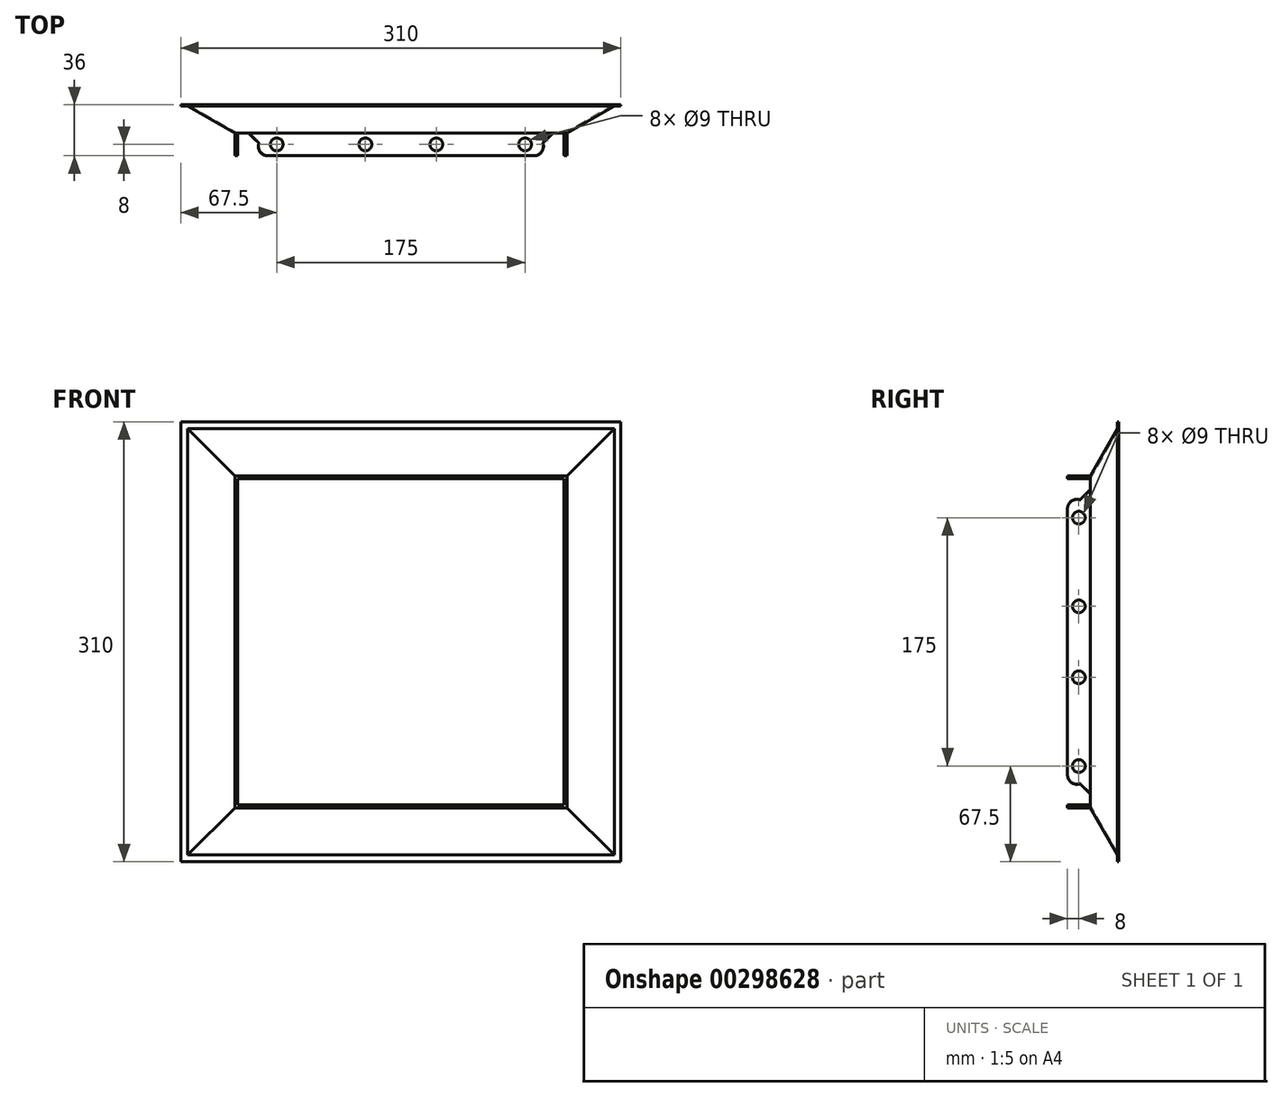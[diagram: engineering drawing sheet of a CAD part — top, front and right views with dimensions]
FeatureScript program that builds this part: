
annotation { "Feature Type Name" : "Feature", "Feature Type Description" : "" }
export const myFeature = defineFeature(function(context is Context, id is Id, definition is map)
    precondition{}
    {
        {
            var Q0;
            Q0=qCreatedBy(makeId("Front.planeOp"),FACE);
            var sketch = newSketch(context, id + "F0", { "sketchPlane" : qUnion([Q0])});
            skLineSegment(sketch, "E0.bottom", {"start": v(-155, 155) * mm, "end": v(155, 155) * mm});
            skLineSegment(sketch, "E0.top", {"start": v(-155, -155) * mm, "end": v(155, -155) * mm});
            skLineSegment(sketch, "E0.left", {"start": v(-155, 155) * mm, "end": v(-155, -155) * mm});
            skLineSegment(sketch, "E0.right", {"start": v(155, 155) * mm, "end": v(155, -155) * mm});
            skLineSegment(sketch, "E1.bottom", {"start": v(150, -150) * mm, "end": v(-150, -150) * mm});
            skLineSegment(sketch, "E1.top", {"start": v(150, 150) * mm, "end": v(-150, 150) * mm});
            skLineSegment(sketch, "E1.left", {"start": v(150, -150) * mm, "end": v(150, 150) * mm});
            skLineSegment(sketch, "E1.right", {"start": v(-150, -150) * mm, "end": v(-150, 150) * mm});
            skPoint(sketch, "E1.middle", {"position": v(0, 0) * mm});
            skSolve(sketch);
        }
        {
            var Q0;
            Q0=makeQuery(id+"F0.imprint","IMPRINT",FACE,{"disambiguationData":[TD([[makeQuery(id+"F0.imprint","IMPRINT",EDGE,{"derivedFrom":sQuery(id+"F0.wireOp",EDGE,"E0.bottom")}),-1.0]])]});
            cPlane(context, id + "F1", {"entities" : qUnion([Q0]), "cplaneType" : CPlaneType.OFFSET, "offset" : 20 * mm, "width" : 150 * mm, "height" : 150 * mm});
        }
        {
            var Q0;
            Q0=qCreatedBy(id+"F1.planeOp",FACE);
            var sketch = newSketch(context, id + "F2", { "sketchPlane" : qUnion([Q0])});
            skLineSegment(sketch, "E2.bottom", {"start": v(115, -115) * mm, "end": v(-115, -115) * mm});
            skLineSegment(sketch, "E2.top", {"start": v(115, 115) * mm, "end": v(-115, 115) * mm});
            skLineSegment(sketch, "E2.left", {"start": v(115, -115) * mm, "end": v(115, 115) * mm});
            skLineSegment(sketch, "E2.right", {"start": v(-115, -115) * mm, "end": v(-115, 115) * mm});
            skPoint(sketch, "E2.middle", {"position": v(0, 0) * mm});
            skSolve(sketch);
        }
        {
            var Q0;
            Q0=makeQuery(id+"F0.imprint","IMPRINT",FACE,{"disambiguationData":[TD([[makeQuery(id+"F0.imprint","IMPRINT",EDGE,{"derivedFrom":sQuery(id+"F0.wireOp",EDGE,"E1.bottom")}),-1.0]])]});
            var Q1;
            Q1=makeQuery(id+"F2.imprint","IMPRINT",FACE,{"disambiguationData":[TD([[makeQuery(id+"F2.imprint","IMPRINT",EDGE,{"derivedFrom":sQuery(id+"F2.wireOp",EDGE,"E2.bottom")}),-1.0]])]});
            loft(context, id + "F3", {"sheetProfilesArray" : [{ "sheetProfileEntities" : qUnion([Q0]) }, { "sheetProfileEntities" : qUnion([Q1]) }]});
        }
        {
            var Q0;
            Q0=makeQuery(id+"F3.opLoft","CAP_FACE",FACE,{"disambiguationData":[OSD([makeQuery(id+"F2.imprint","IMPRINT",FACE,{"disambiguationData":[TD([[makeQuery(id+"F2.imprint","IMPRINT",EDGE,{"derivedFrom":sQuery(id+"F2.wireOp",EDGE,"E2.bottom")}),-1.0]])]})])],"isStart":true});
            var Q1;
            Q1=makeQuery(id+"F3.opLoft","CAP_FACE",FACE,{"disambiguationData":[OSD([makeQuery(id+"F0.imprint","IMPRINT",FACE,{"disambiguationData":[TD([[makeQuery(id+"F0.imprint","IMPRINT",EDGE,{"derivedFrom":sQuery(id+"F0.wireOp",EDGE,"E1.bottom")}),-1.0]])]})])],"isStart":true});
            shell(context, id + "F4", {"entities" : qUnion([Q0, Q1]), "thickness" : 1 * mm, "oppositeDirection" : true});
        }
        {
            var Q0;
            Q0=makeQuery(id+"F0.imprint","IMPRINT",FACE,{"disambiguationData":[TD([[makeQuery(id+"F0.imprint","IMPRINT",EDGE,{"derivedFrom":sQuery(id+"F0.wireOp",EDGE,"E0.bottom")}),-1.0]])]});
            extrude(context, id + "F5", {"entities" : qUnion([Q0]), "operationType" : NewBodyOperationType.ADD, "depth" : 1 * mm});
        }
        {
            var Q0;
            Q0=makeQuery(id+"F3.opLoft","CAP_FACE",FACE,{"disambiguationData":[OSD([makeQuery(id+"F2.imprint","IMPRINT",FACE,{"disambiguationData":[TD([[makeQuery(id+"F2.imprint","IMPRINT",EDGE,{"derivedFrom":sQuery(id+"F2.wireOp",EDGE,"E2.bottom")}),-1.0]])]})])],"isStart":true});
            var sketch = newSketch(context, id + "F6", { "sketchPlane" : qUnion([Q0])});
            skLineSegment(sketch, "E3.0", {"start": v(-115, -115) * mm, "end": v(115, -115) * mm});
            skLineSegment(sketch, "E4.0", {"start": v(115, -115) * mm, "end": v(115, 115) * mm});
            skLineSegment(sketch, "E5.0", {"start": v(117.02, -117.02) * mm, "end": v(117.02, 117.02) * mm});
            skLineSegment(sketch, "E6.0", {"start": v(117.02, 117.02) * mm, "end": v(-117.02, 117.02) * mm});
            skLineSegment(sketch, "E7.0", {"start": v(115, 115) * mm, "end": v(-115, 115) * mm});
            skLineSegment(sketch, "E8.0", {"start": v(-117.02, 117.02) * mm, "end": v(-117.02, -117.02) * mm});
            skLineSegment(sketch, "E9.0", {"start": v(-115, 115) * mm, "end": v(-115, -115) * mm});
            skLineSegment(sketch, "E10.0", {"start": v(-117.02, -117.02) * mm, "end": v(117.02, -117.02) * mm});
            skSolve(sketch);
        }
        {
            var Q0;
            Q0=qSketchRegion(id+"F6",true);
            extrude(context, id + "F7", {"entities" : qUnion([Q0]), "operationType" : NewBodyOperationType.ADD, "depth" : 16 * mm});
        }
        {
            var Q0;
            Q0=makeQuery(id+"F7.opExtrude","SWEPT_FACE",FACE,{"disambiguationData":[OSD([sQuery(id+"F6.wireOp",EDGE,"E6.0")])]});
            var sketch = newSketch(context, id + "F8", { "sketchPlane" : qUnion([Q0])});
            skLineSegment(sketch, "E11", {"start": v(117.02, -20) * mm, "end": v(107.02, -20) * mm});
            skLineSegment(sketch, "E12", {"start": v(107.02, -20) * mm, "end": v(99.94, -27.07) * mm});
            skArc(sketch, "E13", {"start": v(93.63, -36) * mm, "mid": v(99.1, -33.17) * mm, "end": v(99.94, -27.07) * mm});
            skLineSegment(sketch, "E14", {"start": v(117.02, -20) * mm, "end": v(117.02, -36) * mm});
            skLineSegment(sketch, "E15", {"start": v(93.63, -36) * mm, "end": v(117.02, -36) * mm});
            skLineSegment(sketch, "E16", {"start": v(-117.02, -20) * mm, "end": v(-107.02, -20) * mm});
            skLineSegment(sketch, "E17", {"start": v(-107.02, -20) * mm, "end": v(-99.94, -27.07) * mm});
            skArc(sketch, "E18", {"start": v(-99.94, -27.07) * mm, "mid": v(-99.1, -33.17) * mm, "end": v(-93.63, -36) * mm});
            skLineSegment(sketch, "E19", {"start": v(-93.63, -36) * mm, "end": v(-117.02, -36) * mm});
            skLineSegment(sketch, "E20", {"start": v(-117.02, -36) * mm, "end": v(-117.02, -20) * mm});
            skSolve(sketch);
        }
        {
            var Q0;
            Q0=makeQuery(id+"F8.imprint","IMPRINT",FACE,{"disambiguationData":[TD([[makeQuery(id+"F8.imprint","IMPRINT",EDGE,{"derivedFrom":sQuery(id+"F8.wireOp",EDGE,"E11")}),1.0]])]});
            var Q1;
            Q1=sQuery(id+"F8.wireOp",EDGE,"E14");
            revolve(context, id + "F9", {"operationType" : NewBodyOperationType.REMOVE, "entities" : qUnion([Q0]), "axis" : qUnion([Q1]), "revolveType" : RevolveType.FULL, "oppositeDirection" : true});
        }
        {
            var Q0;
            Q0=makeQuery(id+"F8.imprint","IMPRINT",FACE,{"disambiguationData":[TD([[makeQuery(id+"F8.imprint","IMPRINT",EDGE,{"derivedFrom":sQuery(id+"F8.wireOp",EDGE,"E16")}),1.0]])]});
            var Q1;
            Q1=sQuery(id+"F8.wireOp",EDGE,"E20");
            revolve(context, id + "F10", {"operationType" : NewBodyOperationType.REMOVE, "entities" : qUnion([Q0]), "axis" : qUnion([Q1]), "revolveType" : RevolveType.FULL, "oppositeDirection" : true});
        }
        {
            var Q0;
            Q0=makeQuery(id+"F7.opExtrude","SWEPT_FACE",FACE,{"disambiguationData":[OSD([sQuery(id+"F6.wireOp",EDGE,"E10.0")])]});
            var sketch = newSketch(context, id + "F11", { "sketchPlane" : qUnion([Q0])});
            skLineSegment(sketch, "E21.0", {"start": v(-93.63, 36) * mm, "end": v(-117.02, 36) * mm});
            skArc(sketch, "E22.0", {"start": v(-99.94, 27.07) * mm, "mid": v(-99.1, 33.17) * mm, "end": v(-93.63, 36) * mm});
            skLineSegment(sketch, "E22.1", {"start": v(-117.02, 36) * mm, "end": v(-117.02, 20) * mm});
            skLineSegment(sketch, "E22.2", {"start": v(-107.02, 20) * mm, "end": v(-99.94, 27.07) * mm});
            skLineSegment(sketch, "E23.0", {"start": v(-117.02, 20) * mm, "end": v(-107.02, 20) * mm});
            skLineSegment(sketch, "E24.0", {"start": v(93.63, 36) * mm, "end": v(117.02, 36) * mm});
            skLineSegment(sketch, "E25.0", {"start": v(117.02, 20) * mm, "end": v(117.02, 36) * mm});
            skArc(sketch, "E26.0", {"start": v(93.63, 36) * mm, "mid": v(99.1, 33.17) * mm, "end": v(99.94, 27.07) * mm});
            skLineSegment(sketch, "E27.0", {"start": v(107.02, 20) * mm, "end": v(99.94, 27.07) * mm});
            skLineSegment(sketch, "E28.0", {"start": v(117.02, 20) * mm, "end": v(107.02, 20) * mm});
            skSolve(sketch);
        }
        {
            var Q0;
            Q0=makeQuery(id+"F11.imprint","IMPRINT",FACE,{"disambiguationData":[TD([[makeQuery(id+"F11.imprint","IMPRINT",EDGE,{"derivedFrom":sQuery(id+"F11.wireOp",EDGE,"E24.0")}),-1.0]])]});
            var Q1;
            Q1=sQuery(id+"F11.wireOp",EDGE,"E25.0");
            revolve(context, id + "F12", {"operationType" : NewBodyOperationType.REMOVE, "entities" : qUnion([Q0]), "axis" : qUnion([Q1]), "revolveType" : RevolveType.FULL, "oppositeDirection" : true});
        }
        {
            var Q0;
            Q0=makeQuery(id+"F11.imprint","IMPRINT",FACE,{"disambiguationData":[TD([[makeQuery(id+"F11.imprint","IMPRINT",EDGE,{"derivedFrom":sQuery(id+"F11.wireOp",EDGE,"E21.0")}),-1.0]])]});
            var Q1;
            Q1=sQuery(id+"F11.wireOp",EDGE,"E22.1");
            revolve(context, id + "F13", {"operationType" : NewBodyOperationType.REMOVE, "entities" : qUnion([Q0]), "axis" : qUnion([Q1]), "revolveType" : RevolveType.FULL, "oppositeDirection" : true});
        }
        {
            var Q0;
            Q0=makeQuery(id+"F7.opExtrude","SWEPT_FACE",FACE,{"disambiguationData":[OSD([sQuery(id+"F6.wireOp",EDGE,"E5.0")])]});
            var sketch = newSketch(context, id + "F14", { "sketchPlane" : qUnion([Q0])});
            skLineSegment(sketch, "E29", {"start": v(-28, -132.07) * mm, "end": v(-28, 138.05) * mm, "construction": true});
            skCircle(sketch, "E30", {"center": v(-28, -87.5) * mm, "radius": 4.5 * mm});
            skCircle(sketch, "E31", {"center": v(-28, -25) * mm, "radius": 4.5 * mm});
            skCircle(sketch, "E32", {"center": v(-28, 25) * mm, "radius": 4.5 * mm});
            skCircle(sketch, "E33", {"center": v(-28, 87.5) * mm, "radius": 4.5 * mm});
            skSolve(sketch);
        }
        {
            var Q0;
            Q0=makeQuery(id+"F14.imprint","IMPRINT",FACE,{"disambiguationData":[TD([[makeQuery(id+"F14.imprint","IMPRINT",EDGE,{"derivedFrom":sQuery(id+"F14.wireOp",EDGE,"E30")}),1.0]])]});
            var Q1;
            Q1=makeQuery(id+"F14.imprint","IMPRINT",FACE,{"disambiguationData":[TD([[makeQuery(id+"F14.imprint","IMPRINT",EDGE,{"derivedFrom":sQuery(id+"F14.wireOp",EDGE,"E31")}),1.0]])]});
            var Q2;
            Q2=makeQuery(id+"F14.imprint","IMPRINT",FACE,{"disambiguationData":[TD([[makeQuery(id+"F14.imprint","IMPRINT",EDGE,{"derivedFrom":sQuery(id+"F14.wireOp",EDGE,"E32")}),1.0]])]});
            var Q3;
            Q3=makeQuery(id+"F14.imprint","IMPRINT",FACE,{"disambiguationData":[TD([[makeQuery(id+"F14.imprint","IMPRINT",EDGE,{"derivedFrom":sQuery(id+"F14.wireOp",EDGE,"E33")}),1.0]])]});
            extrude(context, id + "F15", {"entities" : qUnion([Q0, Q1, Q2, Q3]), "operationType" : NewBodyOperationType.REMOVE, "endBound" : BoundingType.THROUGH_ALL, "oppositeDirection" : true, "depth" : 25 * mm});
        }
        {
            var Q0;
            Q0=makeQuery(id+"F7.opExtrude","SWEPT_FACE",FACE,{"disambiguationData":[OSD([sQuery(id+"F6.wireOp",EDGE,"E6.0")])]});
            var sketch = newSketch(context, id + "F16", { "sketchPlane" : qUnion([Q0])});
            skLineSegment(sketch, "E34", {"start": v(282.48, -28) * mm, "end": v(-292.8, -28) * mm, "construction": true});
            skCircle(sketch, "E35", {"center": v(87.5, -28) * mm, "radius": 4.5 * mm});
            skCircle(sketch, "E36", {"center": v(25, -28) * mm, "radius": 4.5 * mm});
            skCircle(sketch, "E37", {"center": v(-25, -28) * mm, "radius": 4.5 * mm});
            skCircle(sketch, "E38", {"center": v(-87.5, -28) * mm, "radius": 4.5 * mm});
            skSolve(sketch);
        }
        {
            var Q0;
            Q0=makeQuery(id+"F16.imprint","IMPRINT",FACE,{"disambiguationData":[TD([[makeQuery(id+"F16.imprint","IMPRINT",EDGE,{"derivedFrom":sQuery(id+"F16.wireOp",EDGE,"E35")}),1.0]])]});
            var Q1;
            Q1=makeQuery(id+"F16.imprint","IMPRINT",FACE,{"disambiguationData":[TD([[makeQuery(id+"F16.imprint","IMPRINT",EDGE,{"derivedFrom":sQuery(id+"F16.wireOp",EDGE,"E36")}),1.0]])]});
            var Q2;
            Q2=makeQuery(id+"F16.imprint","IMPRINT",FACE,{"disambiguationData":[TD([[makeQuery(id+"F16.imprint","IMPRINT",EDGE,{"derivedFrom":sQuery(id+"F16.wireOp",EDGE,"E37")}),1.0]])]});
            var Q3;
            Q3=makeQuery(id+"F16.imprint","IMPRINT",FACE,{"disambiguationData":[TD([[makeQuery(id+"F16.imprint","IMPRINT",EDGE,{"derivedFrom":sQuery(id+"F16.wireOp",EDGE,"E38")}),1.0]])]});
            extrude(context, id + "F17", {"entities" : qUnion([Q0, Q1, Q2, Q3]), "operationType" : NewBodyOperationType.REMOVE, "endBound" : BoundingType.THROUGH_ALL, "oppositeDirection" : true, "depth" : 25 * mm});
        }
    });
